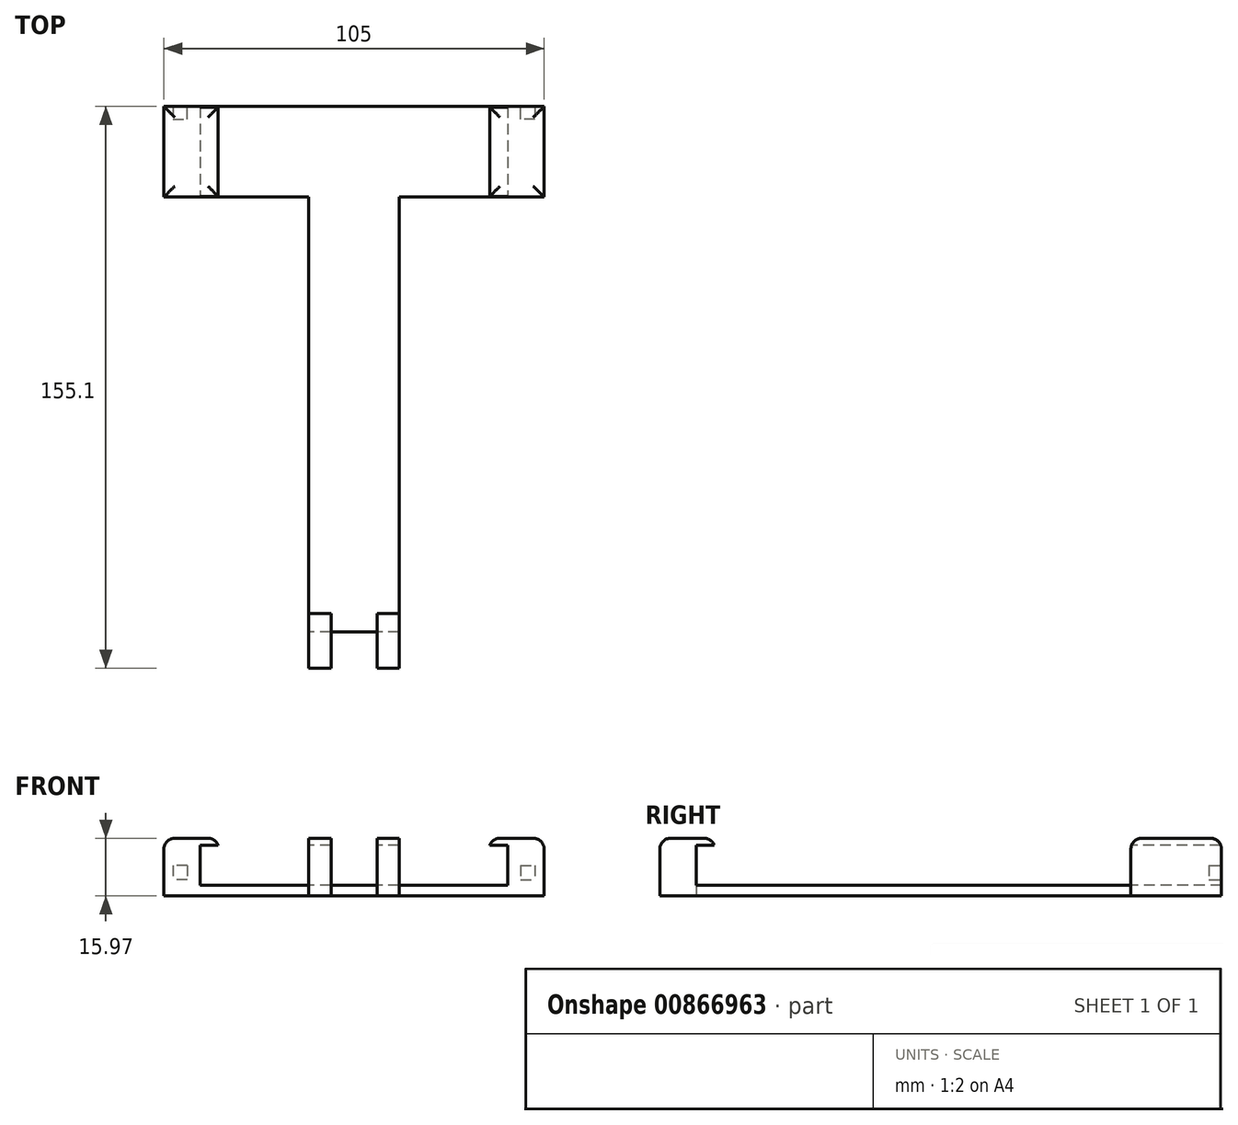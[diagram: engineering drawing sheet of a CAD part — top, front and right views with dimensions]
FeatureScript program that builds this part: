
annotation { "Feature Type Name" : "Feature", "Feature Type Description" : "" }
export const myFeature = defineFeature(function(context is Context, id is Id, definition is map)
    precondition{}
    {
        {
            var Q0;
            Q0=qCreatedBy(makeId("Top.planeOp"),FACE);
            var sketch = newSketch(context, id + "F0", { "sketchPlane" : qUnion([Q0])});
            skLineSegment(sketch, "E0.bottom", {"start": v(12.5, -60.05) * mm, "end": v(-12.5, -60.05) * mm});
            skLineSegment(sketch, "E0.top", {"start": v(12.5, 60.05) * mm, "end": v(-12.5, 60.05) * mm});
            skLineSegment(sketch, "E0.left", {"start": v(12.5, -60.05) * mm, "end": v(12.5, 60.05) * mm});
            skLineSegment(sketch, "E0.right", {"start": v(-12.5, -60.05) * mm, "end": v(-12.5, 60.05) * mm});
            skPoint(sketch, "E0.middle", {"position": v(0, 0) * mm});
            skLineSegment(sketch, "E1", {"start": v(0, 60.05) * mm, "end": v(0, 85.05) * mm});
            skLineSegment(sketch, "E2", {"start": v(0, 85.05) * mm, "end": v(-42.5, 85.05) * mm});
            skLineSegment(sketch, "E3", {"start": v(-42.5, 85.05) * mm, "end": v(-42.5, 60.05) * mm});
            skLineSegment(sketch, "E4", {"start": v(-42.5, 60.05) * mm, "end": v(-12.5, 60.05) * mm});
            skLineSegment(sketch, "E5", {"start": v(0, 85.05) * mm, "end": v(42.5, 85.05) * mm});
            skLineSegment(sketch, "E6", {"start": v(42.5, 85.05) * mm, "end": v(42.5, 60.05) * mm});
            skLineSegment(sketch, "E7", {"start": v(42.5, 60.05) * mm, "end": v(12.5, 60.05) * mm});
            skLineSegment(sketch, "E8", {"start": v(42.5, 85.05) * mm, "end": v(52.5, 85.05) * mm});
            skLineSegment(sketch, "E9", {"start": v(52.5, 85.05) * mm, "end": v(52.5, 60.05) * mm});
            skLineSegment(sketch, "E10", {"start": v(52.5, 60.05) * mm, "end": v(42.5, 60.05) * mm});
            skLineSegment(sketch, "E11", {"start": v(37.5, 85.05) * mm, "end": v(37.5, 60.05) * mm});
            skLineSegment(sketch, "E12", {"start": v(-37.5, 85.05) * mm, "end": v(-37.5, 60.05) * mm});
            skLineSegment(sketch, "E13", {"start": v(-42.5, 85.05) * mm, "end": v(-52.5, 85.05) * mm});
            skLineSegment(sketch, "E14", {"start": v(-52.5, 85.05) * mm, "end": v(-52.5, 60.05) * mm});
            skLineSegment(sketch, "E15", {"start": v(-52.5, 60.05) * mm, "end": v(-42.5, 60.05) * mm});
            skLineSegment(sketch, "E16", {"start": v(-19.54, -60.05) * mm, "end": v(-19.54, -55.05) * mm});
            skLineSegment(sketch, "E17", {"start": v(-12.5, -60.05) * mm, "end": v(-12.5, -70.05) * mm});
            skLineSegment(sketch, "E18", {"start": v(-12.5, -70.05) * mm, "end": v(12.5, -70.05) * mm});
            skLineSegment(sketch, "E19", {"start": v(12.5, -70.05) * mm, "end": v(12.5, -60.05) * mm});
            skLineSegment(sketch, "E20", {"start": v(-12.5, -55.05) * mm, "end": v(12.5, -55.05) * mm});
            skLineSegment(sketch, "E21", {"start": v(-6.35, -55.05) * mm, "end": v(-6.35, -70.05) * mm});
            skLineSegment(sketch, "E22", {"start": v(6.35, -55.05) * mm, "end": v(6.35, -70.05) * mm});
            skLineSegment(sketch, "E23", {"start": v(-50, 85.05) * mm, "end": v(-50, 81.55) * mm});
            skLineSegment(sketch, "E24", {"start": v(-50, 81.55) * mm, "end": v(-46, 81.55) * mm});
            skLineSegment(sketch, "E25", {"start": v(-46, 81.55) * mm, "end": v(-46, 85.05) * mm});
            skLineSegment(sketch, "E26.MirrorCS", {"start": v(50, 85.05) * mm, "end": v(50, 81.55) * mm});
            skLineSegment(sketch, "E27.MirrorCS", {"start": v(50, 81.55) * mm, "end": v(46, 81.55) * mm});
            skLineSegment(sketch, "E28.MirrorCS", {"start": v(46, 81.55) * mm, "end": v(46, 85.05) * mm});
            skSolve(sketch);
        }
        {
            var Q0;
            {var subQ0=sQuery(id+"F0.wireOp",EDGE,"E0.bottom");Q0=makeQuery(id+"F0.imprint","IMPRINT",FACE,{"disambiguationData":[TD([[makeQuery(id+"F0.imprint","IMPRINT",EDGE,{"derivedFrom":subQ0}),-1.0]])]});}
            var Q1;
            {var subQ0=sQuery(id+"F0.wireOp",EDGE,"E3");Q1=makeQuery(id+"F0.imprint","IMPRINT",FACE,{"disambiguationData":[TD([[makeQuery(id+"F0.imprint","IMPRINT",EDGE,{"derivedFrom":subQ0}),1.0]])]});}
            var Q2;
            {var subQ0=sQuery(id+"F0.wireOp",EDGE,"E6");Q2=makeQuery(id+"F0.imprint","IMPRINT",FACE,{"disambiguationData":[TD([[makeQuery(id+"F0.imprint","IMPRINT",EDGE,{"derivedFrom":subQ0}),-1.0]])]});}
            var Q3;
            {var subQ3=sQuery(id+"F0.wireOp",EDGE,"E20");Q3=makeQuery(id+"F0.imprint","IMPRINT",FACE,{"disambiguationData":[TD([[makeQuery(id+"F0.imprint","IMPRINT",EDGE,{"derivedFrom":subQ3}),1.0]])]});}
            var Q4;
            {var subQ1=sQuery(id+"F0.wireOp",EDGE,"E1");Q4=makeQuery(id+"F0.imprint","IMPRINT",FACE,{"disambiguationData":[TD([[makeQuery(id+"F0.imprint","IMPRINT",EDGE,{"derivedFrom":subQ1}),-1.0]])]});}
            var Q5;
            {var subQ1=sQuery(id+"F0.wireOp",EDGE,"E1");Q5=makeQuery(id+"F0.imprint","IMPRINT",FACE,{"disambiguationData":[TD([[makeQuery(id+"F0.imprint","IMPRINT",EDGE,{"derivedFrom":subQ1}),1.0]])]});}
            extrude(context, id + "F1", {"entities" : qUnion([Q0, Q1, Q2, Q3, Q4, Q5]), "depth" : 3 * mm, "offsetDistance" : 25 * mm});
        }
        {
            var Q0;
            Q0=makeQuery(id+"F0.imprint","IMPRINT",FACE,{"disambiguationData":[TD([[makeQuery(id+"F0.imprint","IMPRINT",EDGE,{"derivedFrom":sQuery(id+"F0.wireOp",EDGE,"E3")}),-1.0]])]});
            var Q1;
            Q1=makeQuery(id+"F0.imprint","IMPRINT",FACE,{"disambiguationData":[TD([[makeQuery(id+"F0.imprint","IMPRINT",EDGE,{"derivedFrom":sQuery(id+"F0.wireOp",EDGE,"E6")}),1.0]])]});
            var Q2;
            {var subQ0=sQuery(id+"F0.wireOp",EDGE,"E19");Q2=makeQuery(id+"F0.imprint","IMPRINT",FACE,{"disambiguationData":[TD([[makeQuery(id+"F0.imprint","IMPRINT",EDGE,{"derivedFrom":subQ0}),1.0]])]});}
            var Q3;
            {var subQ0=sQuery(id+"F0.wireOp",EDGE,"E17");Q3=makeQuery(id+"F0.imprint","IMPRINT",FACE,{"disambiguationData":[TD([[makeQuery(id+"F0.imprint","IMPRINT",EDGE,{"derivedFrom":subQ0}),1.0]])]});}
            var Q4;
            {var subQ0=sQuery(id+"F0.wireOp",EDGE,"E23");Q4=makeQuery(id+"F0.imprint","IMPRINT",FACE,{"disambiguationData":[TD([[makeQuery(id+"F0.imprint","IMPRINT",EDGE,{"derivedFrom":subQ0}),1.0]])]});}
            var Q5;
            {var subQ0=sQuery(id+"F0.wireOp",EDGE,"E26.MirrorCS");Q5=makeQuery(id+"F0.imprint","IMPRINT",FACE,{"disambiguationData":[TD([[makeQuery(id+"F0.imprint","IMPRINT",EDGE,{"derivedFrom":subQ0}),-1.0]])]});}
            extrude(context, id + "F2", {"entities" : qUnion([Q0, Q1, Q2, Q3, Q4, Q5]), "operationType" : NewBodyOperationType.ADD, "depth" : ((0.55 * 2.54 * 10) + 2) * mm, "offsetDistance" : 25 * mm});
        }
        {
            var Q0;
            {var subQ0=sQuery(id+"F0.wireOp",EDGE,"E3");Q0=makeQuery(id+"F0.imprint","IMPRINT",FACE,{"disambiguationData":[TD([[makeQuery(id+"F0.imprint","IMPRINT",EDGE,{"derivedFrom":subQ0}),1.0]])]});}
            var Q1;
            {var subQ0=sQuery(id+"F0.wireOp",EDGE,"E6");Q1=makeQuery(id+"F0.imprint","IMPRINT",FACE,{"disambiguationData":[TD([[makeQuery(id+"F0.imprint","IMPRINT",EDGE,{"derivedFrom":subQ0}),-1.0]])]});}
            var Q2;
            {var subQ0=sQuery(id+"F0.wireOp",EDGE,"E0.right");var subQ5=sQuery(id+"F0.wireOp",EDGE,"E20");var subQ6=makeQuery(id+"F0.imprint","INTERSECT",VERTEX,{"derivedFrom":[subQ0,subQ5]});Q2=makeQuery(id+"F0.imprint","IMPRINT",FACE,{"disambiguationData":[TD([[makeQuery(id+"F0.imprint","IMPRINT",EDGE,{"disambiguationData":[TD([[subQ6,-1.0]])],"derivedFrom":subQ5}),-1.0]])]});}
            var Q3;
            {var subQ0=sQuery(id+"F0.wireOp",EDGE,"E0.left");var subQ5=sQuery(id+"F0.wireOp",EDGE,"E20");var subQ6=makeQuery(id+"F0.imprint","INTERSECT",VERTEX,{"derivedFrom":[subQ0,subQ5]});Q3=makeQuery(id+"F0.imprint","IMPRINT",FACE,{"disambiguationData":[TD([[makeQuery(id+"F0.imprint","IMPRINT",EDGE,{"disambiguationData":[TD([[subQ6,1.0]])],"derivedFrom":subQ5}),-1.0]])]});}
            extrude(context, id + "F3", {"entities" : qUnion([Q0, Q1, Q2, Q3]), "operationType" : NewBodyOperationType.ADD, "depth" : 15.97 * mm, "offsetDistance" : 25 * mm, "hasSecondDirection" : true, "secondDirectionOppositeDirection" : false, "secondDirectionDepth" : 13.97 * mm});
        }
        {
            var Q0;
            {var subQ0=sQuery(id+"F0.wireOp",EDGE,"E18");Q0=makeQuery(id+"F2.opExtrude","CAP_EDGE",EDGE,{"disambiguationData":[OSD([subQ0]),TDD([makeQuery(id+"F0.imprint","IMPRINT",EDGE,{"disambiguationData":[TD([[makeQuery(id+"F0.imprint","INTERSECT",VERTEX,{"derivedFrom":[sQuery(id+"F0.wireOp",EDGE,"E17"),subQ0]}),-1.0]])],"derivedFrom":subQ0})])],"isStart":false});}
            var Q1;
            {var subQ0=sQuery(id+"F0.wireOp",EDGE,"E18");Q1=makeQuery(id+"F2.opExtrude","CAP_EDGE",EDGE,{"disambiguationData":[OSD([subQ0]),TDD([makeQuery(id+"F0.imprint","IMPRINT",EDGE,{"disambiguationData":[TD([[makeQuery(id+"F0.imprint","INTERSECT",VERTEX,{"derivedFrom":[subQ0,sQuery(id+"F0.wireOp",EDGE,"E19")]}),1.0]])],"derivedFrom":subQ0})])],"isStart":false});}
            var Q2;
            Q2=makeQuery(id+"F3.boolean.opBoolean","MERGE",EDGE,{"derivedFrom":[makeQuery(id+"F2.opExtrude","CAP_EDGE",EDGE,{"disambiguationData":[OSD([sQuery(id+"F0.wireOp",EDGE,"E10")])],"isStart":false}),makeQuery(id+"F3.opExtrude","CAP_EDGE",EDGE,{"disambiguationData":[OSD([sQuery(id+"F0.wireOp",EDGE,"E7")])],"isStart":false})]});
            var Q3;
            Q3=makeQuery(id+"F2.opExtrude","CAP_EDGE",EDGE,{"disambiguationData":[OSD([sQuery(id+"F0.wireOp",EDGE,"E9")])],"isStart":false});
            var Q4;
            Q4=makeQuery(id+"F3.boolean.opBoolean","MERGE",EDGE,{"derivedFrom":[makeQuery(id+"F2.opExtrude","CAP_EDGE",EDGE,{"disambiguationData":[OSD([sQuery(id+"F0.wireOp",EDGE,"E15")])],"isStart":false}),makeQuery(id+"F3.opExtrude","CAP_EDGE",EDGE,{"disambiguationData":[OSD([sQuery(id+"F0.wireOp",EDGE,"E4")])],"isStart":false})]});
            var Q5;
            Q5=makeQuery(id+"F2.opExtrude","CAP_EDGE",EDGE,{"disambiguationData":[OSD([sQuery(id+"F0.wireOp",EDGE,"E14")])],"isStart":false});
            var Q6;
            Q6=makeQuery(id+"F3.boolean.opBoolean","MERGE",EDGE,{"derivedFrom":[makeQuery(id+"F2.opExtrude","CAP_EDGE",EDGE,{"disambiguationData":[OSD([sQuery(id+"F0.wireOp",EDGE,"E13")])],"isStart":false}),makeQuery(id+"F3.opExtrude","CAP_EDGE",EDGE,{"disambiguationData":[OSD([sQuery(id+"F0.wireOp",EDGE,"E2")])],"isStart":false})]});
            var Q7;
            Q7=makeQuery(id+"F3.boolean.opBoolean","MERGE",EDGE,{"derivedFrom":[makeQuery(id+"F2.opExtrude","CAP_EDGE",EDGE,{"disambiguationData":[OSD([sQuery(id+"F0.wireOp",EDGE,"E8")])],"isStart":false}),makeQuery(id+"F3.opExtrude","CAP_EDGE",EDGE,{"disambiguationData":[OSD([sQuery(id+"F0.wireOp",EDGE,"E5")])],"isStart":false})]});
            var Q8;
            Q8=makeQuery(id+"F3.opExtrude","CAP_EDGE",EDGE,{"disambiguationData":[OSD([sQuery(id+"F0.wireOp",EDGE,"E11")])],"isStart":false});
            var Q9;
            Q9=makeQuery(id+"F3.opExtrude","CAP_EDGE",EDGE,{"disambiguationData":[OSD([sQuery(id+"F0.wireOp",EDGE,"E12")])],"isStart":false});
            var Q10;
            {var subQ0=sQuery(id+"F0.wireOp",EDGE,"E20");Q10=makeQuery(id+"F3.opExtrude","CAP_EDGE",EDGE,{"disambiguationData":[OSD([subQ0]),TDD([makeQuery(id+"F0.imprint","IMPRINT",EDGE,{"disambiguationData":[TD([[makeQuery(id+"F0.imprint","INTERSECT",VERTEX,{"derivedFrom":[sQuery(id+"F0.wireOp",EDGE,"E0.right"),subQ0]}),-1.0]])],"derivedFrom":subQ0})])],"isStart":false});}
            var Q11;
            {var subQ0=sQuery(id+"F0.wireOp",EDGE,"E20");Q11=makeQuery(id+"F3.opExtrude","CAP_EDGE",EDGE,{"disambiguationData":[OSD([subQ0]),TDD([makeQuery(id+"F0.imprint","IMPRINT",EDGE,{"disambiguationData":[TD([[makeQuery(id+"F0.imprint","INTERSECT",VERTEX,{"derivedFrom":[sQuery(id+"F0.wireOp",EDGE,"E0.left"),subQ0]}),1.0]])],"derivedFrom":subQ0})])],"isStart":false});}
            fillet(context, id + "F4", {"entities" : qUnion([Q0, Q1, Q2, Q3, Q4, Q5, Q6, Q7, Q8, Q9, Q10, Q11]), "radius" : 3 * mm, "tangentPropagation" : true, "allowEdgeOverflow" : false});
        }
        {
            var Q0;
            {var subQ0=sQuery(id+"F0.wireOp",EDGE,"E23");Q0=makeQuery(id+"F0.imprint","IMPRINT",FACE,{"disambiguationData":[TD([[makeQuery(id+"F0.imprint","IMPRINT",EDGE,{"derivedFrom":subQ0}),1.0]])]});}
            var Q1;
            {var subQ0=sQuery(id+"F0.wireOp",EDGE,"E26.MirrorCS");Q1=makeQuery(id+"F0.imprint","IMPRINT",FACE,{"disambiguationData":[TD([[makeQuery(id+"F0.imprint","IMPRINT",EDGE,{"derivedFrom":subQ0}),-1.0]])]});}
            extrude(context, id + "F5", {"entities" : qUnion([Q0, Q1]), "operationType" : NewBodyOperationType.REMOVE, "depth" : (5 + 3.5) * mm, "offsetDistance" : 25 * mm, "hasSecondDirection" : true, "secondDirectionOppositeDirection" : false, "secondDirectionDepth" : (5 - 0.5) * mm});
        }
    });
